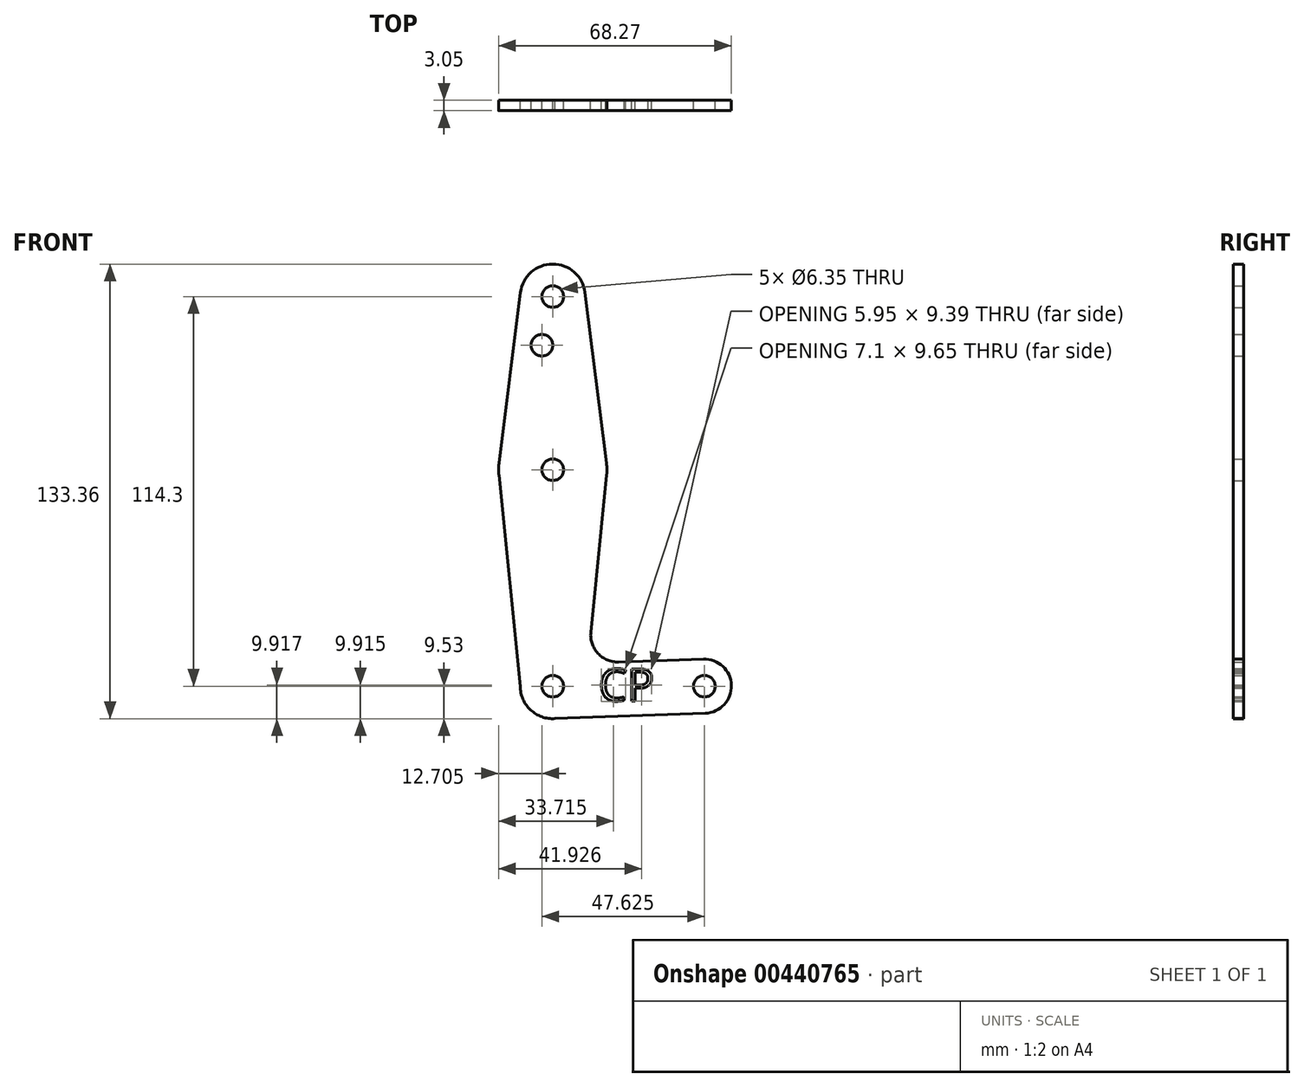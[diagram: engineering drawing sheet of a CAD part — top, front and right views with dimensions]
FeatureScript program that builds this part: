
annotation { "Feature Type Name" : "Feature", "Feature Type Description" : "" }
export const myFeature = defineFeature(function(context is Context, id is Id, definition is map)
    precondition{}
    {
        {
            var Q0;
            Q0=qCreatedBy(makeId("Front.planeOp"),FACE);
            var sketch = newSketch(context, id + "F0", { "sketchPlane" : qUnion([Q0])});
            skLineSegment(sketch, "E0", {"start": v(0, 0) * mm, "end": v(44.45, 0) * mm, "construction": true});
            skLineSegment(sketch, "E1", {"start": v(0, 0) * mm, "end": v(0, 114.3) * mm, "construction": true});
            skCircle(sketch, "E2", {"center": v(0, 0) * mm, "radius": 9.52 * mm});
            skCircle(sketch, "E3", {"center": v(0, 114.3) * mm, "radius": 9.52 * mm});
            skCircle(sketch, "E4", {"center": v(0, 63.5) * mm, "radius": 15.88 * mm});
            skCircle(sketch, "E5", {"center": v(44.45, 0) * mm, "radius": 7.94 * mm});
            skLineSegment(sketch, "E6", {"start": v(-9.45, 115.5) * mm, "end": v(-15.75, 65.48) * mm});
            skCircle(sketch, "E7", {"center": v(0, 114.3) * mm, "radius": 3.18 * mm});
            skCircle(sketch, "E8", {"center": v(0, 63.5) * mm, "radius": 3.18 * mm});
            skCircle(sketch, "E9", {"center": v(0, 0) * mm, "radius": 3.18 * mm});
            skCircle(sketch, "E10", {"center": v(44.45, 0) * mm, "radius": 3.18 * mm});
            skCircle(sketch, "E11", {"center": v(-3.18, 100.03) * mm, "radius": 3.18 * mm});
            skPoint(sketch, "E11.centerSnap0", {"position": v(11.4, 100.03) * mm});
            skLineSegment(sketch, "E12", {"start": v(9.45, 115.5) * mm, "end": v(15.75, 65.48) * mm});
            skLineSegment(sketch, "E13", {"start": v(0, -9.52) * mm, "end": v(44.73, -7.93) * mm});
            skLineSegment(sketch, "E14", {"start": v(15.8, 61.91) * mm, "end": v(11.16, 15.84) * mm});
            skLineSegment(sketch, "E15", {"start": v(19.34, 7.1) * mm, "end": v(44.18, 7.93) * mm});
            skLineSegment(sketch, "E16", {"start": v(-9.52, 0) * mm, "end": v(-15.8, 61.9) * mm});
            skPoint(sketch, "E17.newPointA", {"position": v(9.57, 0) * mm});
            skArc(sketch, "E17.filletArc", {"start": v(11.16, 15.84) * mm, "mid": v(13.27, 9.61) * mm, "end": v(19.34, 7.1) * mm});
            skText(sketch, "E18", { "text": "CP", "fontName": "OpenSans-Regular.ttf"});
            skPoint(sketch, "E18.firstSnap0", {"position": v(13.48, 38.88) * mm});
            const initialGuessF0  = {"E18": [0.01348, -0.00431, 1, 0, 0.00947]};
            skSetInitialGuess(sketch, initialGuessF0);
            skSolve(sketch);
        }
        {
            var Q0;
            Q0 = qSketchRegion(id + "F0", true);
            var Q1;
            Q1=makeQuery(id+"F0.imprint","IMPRINT",FACE,{"disambiguationData":[TD([[makeQuery(id+"F0.imprint","IMPRINT",EDGE,{"derivedFrom":sQuery(id+"F0.wireOp",EDGE,"E18.sketch_text.stroke-23")}),1.0]])]});
            extrude(context, id + "F1", {"entities" : qUnion([Q0, Q1]), "depth" : 3.05 * mm});
        }
    });
